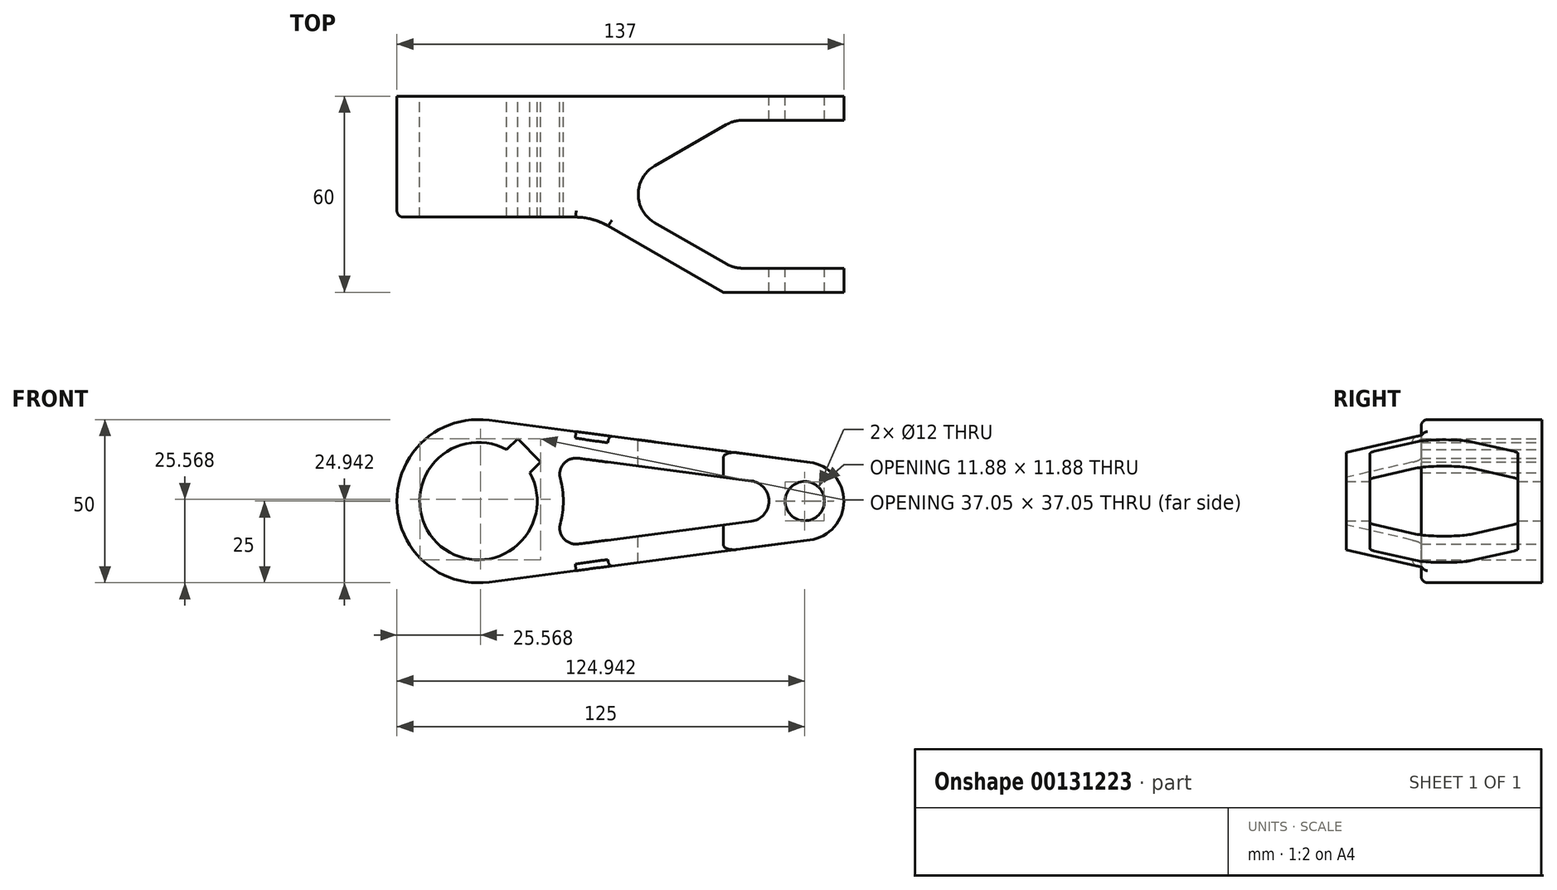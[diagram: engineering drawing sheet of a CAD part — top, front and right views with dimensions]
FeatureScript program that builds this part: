
annotation { "Feature Type Name" : "Feature", "Feature Type Description" : "" }
export const myFeature = defineFeature(function(context is Context, id is Id, definition is map)
    precondition{}
    {
        {
            var Q0;
            Q0=qCreatedBy(makeId("Front.planeOp"),FACE);
            var sketch = newSketch(context, id + "F0", { "sketchPlane" : qUnion([Q0])});
            skArc(sketch, "E0", {"start": v(3.25, 24.79) * mm, "mid": v(-25, 0) * mm, "end": v(3.25, -24.79) * mm});
            skArc(sketch, "E1", {"start": v(101.56, -11.9) * mm, "mid": v(112, 0) * mm, "end": v(101.56, 11.9) * mm});
            skLineSegment(sketch, "E2", {"start": v(0, 0) * mm, "end": v(100, 0) * mm, "construction": true});
            skLineSegment(sketch, "E3", {"start": v(3.25, 24.79) * mm, "end": v(101.56, 11.9) * mm});
            skLineSegment(sketch, "E4", {"start": v(3.25, -24.79) * mm, "end": v(101.56, -11.9) * mm});
            skArc(sketch, "E5", {"start": v(8.7, 15.76) * mm, "mid": v(-12.73, -12.73) * mm, "end": v(15.76, 8.7) * mm});
            skCircle(sketch, "E6", {"center": v(100, 0) * mm, "radius": 6 * mm});
            skLineSegment(sketch, "E7.0", {"start": v(30.55, 13.14) * mm, "end": v(83.57, 6.19) * mm});
            skArc(sketch, "E8.0", {"start": v(26, 0) * mm, "mid": v(25.77, 3.46) * mm, "end": v(25.08, 6.86) * mm});
            skPoint(sketch, "E9.visualSharp", {"position": v(21.72, 14.3) * mm});
            skArc(sketch, "E9.filletArc", {"start": v(30.55, 13.14) * mm, "mid": v(26.13, 11.47) * mm, "end": v(25.08, 6.86) * mm});
            skArc(sketch, "E10", {"start": v(89, 0) * mm, "mid": v(87.45, 4.12) * mm, "end": v(83.57, 6.19) * mm});
            skArc(sketch, "E11.MirrorCS", {"start": v(89, 0) * mm, "mid": v(87.45, -4.12) * mm, "end": v(83.57, -6.19) * mm});
            skLineSegment(sketch, "E12.MirrorCS", {"start": v(30.55, -13.14) * mm, "end": v(83.57, -6.19) * mm});
            skArc(sketch, "E13.MirrorCS", {"start": v(30.55, -13.14) * mm, "mid": v(26.13, -11.47) * mm, "end": v(25.08, -6.86) * mm});
            skArc(sketch, "E14.MirrorCS", {"start": v(26, 0) * mm, "mid": v(25.77, -3.46) * mm, "end": v(25.08, -6.86) * mm});
            skLineSegment(sketch, "E15", {"start": v(0, 0) * mm, "end": v(17.17, 17.17) * mm, "construction": true});
            skLineSegment(sketch, "E16", {"start": v(15.76, 8.7) * mm, "end": v(19.1, 12.02) * mm});
            skLineSegment(sketch, "E17", {"start": v(12.02, 19.1) * mm, "end": v(8.7, 15.76) * mm});
            skLineSegment(sketch, "E18", {"start": v(12.02, 19.1) * mm, "end": v(19.1, 12.02) * mm});
            skSolve(sketch);
        }
        {
            var Q0;
            Q0 = qSketchRegion(id + "F0", true);
            extrude(context, id + "F1", {"entities" : qUnion([Q0]), "endBound" : BoundingType.SYMMETRIC, "depth" : 60 * mm});
        }
        {
            var Q0;
            Q0=qCreatedBy(makeId("Top.planeOp"),FACE);
            var sketch = newSketch(context, id + "F2", { "sketchPlane" : qUnion([Q0])});
            skLineSegment(sketch, "E19", {"start": v(-36.02, 0) * mm, "end": v(127.3, 0) * mm, "construction": true});
            skLineSegment(sketch, "E20", {"start": v(-25, -7) * mm, "end": v(35, -7) * mm});
            skLineSegment(sketch, "E21", {"start": v(35, -7) * mm, "end": v(75, -30) * mm});
            skLineSegment(sketch, "E22", {"start": v(-25, -30) * mm, "end": v(-25, 30) * mm, "construction": true});
            skLineSegment(sketch, "E23", {"start": v(-25, -7) * mm, "end": v(-25, -30) * mm});
            skLineSegment(sketch, "E24", {"start": v(75, -30) * mm, "end": v(-25, -30) * mm});
            skSolve(sketch);
        }
        {
            var Q0;
            Q0 = qSketchRegion(id + "F2", true);
            extrude(context, id + "F3", {"entities" : qUnion([Q0]), "operationType" : NewBodyOperationType.REMOVE, "endBound" : BoundingType.THROUGH_ALL, "oppositeDirection" : true, "depth" : 25 * mm, "hasSecondDirection" : true, "secondDirectionBound" : SecondDirectionBoundingType.THROUGH_ALL, "secondDirectionOppositeDirection" : false, "secondDirectionDepth" : 25 * mm});
        }
        {
            var Q0;
            Q0=qCreatedBy(makeId("Top.planeOp"),FACE);
            var sketch = newSketch(context, id + "F4", { "sketchPlane" : qUnion([Q0])});
            skLineSegment(sketch, "E25.0.0", {"start": v(101.56, 30) * mm, "end": v(112, 30) * mm, "construction": true});
            skLineSegment(sketch, "E25.0.1", {"start": v(101.56, 30) * mm, "end": v(101.56, -30) * mm, "construction": true});
            skLineSegment(sketch, "E25.0.2", {"start": v(101.56, -30) * mm, "end": v(112, -30) * mm, "construction": true});
            skLineSegment(sketch, "E25.0.3", {"start": v(101.56, -30) * mm, "end": v(101.56, 30) * mm, "construction": true});
            skLineSegment(sketch, "E26", {"start": v(112, 30) * mm, "end": v(112, -30) * mm, "construction": true});
            skLineSegment(sketch, "E27", {"start": v(112, -22.65) * mm, "end": v(78.27, -22.65) * mm});
            skLineSegment(sketch, "E28", {"start": v(78.27, -22.65) * mm, "end": v(38.88, 0) * mm});
            skLineSegment(sketch, "E29", {"start": v(38.88, 0) * mm, "end": v(0, 0) * mm, "construction": true});
            skLineSegment(sketch, "E30.MirrorCS", {"start": v(78.27, 22.65) * mm, "end": v(38.88, 0) * mm});
            skLineSegment(sketch, "E31.MirrorCS", {"start": v(112, 22.65) * mm, "end": v(78.27, 22.65) * mm});
            skLineSegment(sketch, "E32", {"start": v(112, 22.65) * mm, "end": v(112, -22.65) * mm});
            skSolve(sketch);
        }
        {
            var Q0;
            Q0 = qSketchRegion(id + "F4", true);
            extrude(context, id + "F5", {"entities" : qUnion([Q0]), "operationType" : NewBodyOperationType.REMOVE, "endBound" : BoundingType.THROUGH_ALL, "oppositeDirection" : true, "depth" : 25 * mm, "hasSecondDirection" : true, "secondDirectionBound" : SecondDirectionBoundingType.THROUGH_ALL, "secondDirectionOppositeDirection" : false, "secondDirectionDepth" : 25 * mm});
        }
        {
            var Q0;
            Q0=makeQuery(id+"F5.boolean.opBoolean","COPY",EDGE,{"disambiguationData":[OD(0.0)],"derivedFrom":makeQuery(id+"F5.opExtrude","SWEPT_EDGE",EDGE,{"disambiguationData":[OSD([sQuery(id+"F4.wireOp",EDGE,"E28"),sQuery(id+"F4.wireOp",EDGE,"E30.MirrorCS")])]})});
            var Q1;
            Q1=makeQuery(id+"F5.boolean.opBoolean","COPY",EDGE,{"disambiguationData":[OD(0.0)],"derivedFrom":makeQuery(id+"F5.opExtrude","SWEPT_EDGE",EDGE,{"disambiguationData":[OSD([sQuery(id+"F4.wireOp",EDGE,"E27"),sQuery(id+"F4.wireOp",EDGE,"E28")])]})});
            var Q2;
            Q2=makeQuery(id+"F5.boolean.opBoolean","COPY",EDGE,{"disambiguationData":[OD(1.0)],"derivedFrom":makeQuery(id+"F5.opExtrude","SWEPT_EDGE",EDGE,{"disambiguationData":[OSD([sQuery(id+"F4.wireOp",EDGE,"E27"),sQuery(id+"F4.wireOp",EDGE,"E28")])]})});
            var Q3;
            Q3=makeQuery(id+"F5.boolean.opBoolean","COPY",EDGE,{"disambiguationData":[OD(0.0)],"derivedFrom":makeQuery(id+"F5.opExtrude","SWEPT_EDGE",EDGE,{"disambiguationData":[OSD([sQuery(id+"F4.wireOp",EDGE,"E30.MirrorCS"),sQuery(id+"F4.wireOp",EDGE,"E31.MirrorCS")])]})});
            var Q4;
            Q4=makeQuery(id+"F5.boolean.opBoolean","COPY",EDGE,{"disambiguationData":[OD(1.0)],"derivedFrom":makeQuery(id+"F5.opExtrude","SWEPT_EDGE",EDGE,{"disambiguationData":[OSD([sQuery(id+"F4.wireOp",EDGE,"E30.MirrorCS"),sQuery(id+"F4.wireOp",EDGE,"E31.MirrorCS")])]})});
            var Q5;
            Q5=makeQuery(id+"F5.boolean.opBoolean","COPY",EDGE,{"disambiguationData":[OD(1.0)],"derivedFrom":makeQuery(id+"F5.opExtrude","SWEPT_EDGE",EDGE,{"disambiguationData":[OSD([sQuery(id+"F4.wireOp",EDGE,"E28"),sQuery(id+"F4.wireOp",EDGE,"E30.MirrorCS")])]})});
            fillet(context, id + "F6", {"entities" : qUnion([Q0, Q1, Q2, Q3, Q4, Q5]), "radius" : 10 * mm, "tangentPropagation" : true, "allowEdgeOverflow" : false});
        }
        {
            var Q0;
            Q0=makeQuery(id+"F3.boolean.opBoolean","COPY",EDGE,{"disambiguationData":[OD(0.0)],"derivedFrom":makeQuery(id+"F3.opExtrude","SWEPT_EDGE",EDGE,{"disambiguationData":[OSD([sQuery(id+"F2.wireOp",EDGE,"E20"),sQuery(id+"F2.wireOp",EDGE,"E21")])]})});
            var Q1;
            Q1=makeQuery(id+"F3.boolean.opBoolean","COPY",EDGE,{"disambiguationData":[OD(1.0)],"derivedFrom":makeQuery(id+"F3.opExtrude","SWEPT_EDGE",EDGE,{"disambiguationData":[OSD([sQuery(id+"F2.wireOp",EDGE,"E20"),sQuery(id+"F2.wireOp",EDGE,"E21")])]})});
            var Q2;
            Q2=makeQuery(id+"F3.boolean.opBoolean","COPY",EDGE,{"disambiguationData":[OD(1.0)],"derivedFrom":makeQuery(id+"F3.opExtrude","SWEPT_EDGE",EDGE,{"disambiguationData":[OSD([sQuery(id+"F2.wireOp",EDGE,"E21"),sQuery(id+"F2.wireOp",EDGE,"E24")])]})});
            var Q3;
            Q3=makeQuery(id+"F3.boolean.opBoolean","COPY",EDGE,{"disambiguationData":[OD(0.0)],"derivedFrom":makeQuery(id+"F3.opExtrude","SWEPT_EDGE",EDGE,{"disambiguationData":[OSD([sQuery(id+"F2.wireOp",EDGE,"E21"),sQuery(id+"F2.wireOp",EDGE,"E24")])]})});
            var Q4;
            Q4=makeQuery(id+"FLbMQRUbMm99wUV_1.1.F3.boolean.opBoolean","COPY",EDGE,{"disambiguationData":[OD(0.0)],"derivedFrom":makeQuery(id+"FLbMQRUbMm99wUV_1.1.F3.opExtrude","SWEPT_EDGE",EDGE,{"disambiguationData":[OSD([sQuery(id+"F2.wireOp",EDGE,"E20"),sQuery(id+"F2.wireOp",EDGE,"E21")])]})});
            var Q5;
            Q5=makeQuery(id+"FLbMQRUbMm99wUV_1.1.F3.boolean.opBoolean","COPY",EDGE,{"disambiguationData":[OD(1.0)],"derivedFrom":makeQuery(id+"FLbMQRUbMm99wUV_1.1.F3.opExtrude","SWEPT_EDGE",EDGE,{"disambiguationData":[OSD([sQuery(id+"F2.wireOp",EDGE,"E20"),sQuery(id+"F2.wireOp",EDGE,"E21")])]})});
            var Q6;
            Q6=makeQuery(id+"FLbMQRUbMm99wUV_1.1.F3.boolean.opBoolean","COPY",EDGE,{"disambiguationData":[OD(0.0)],"derivedFrom":makeQuery(id+"FLbMQRUbMm99wUV_1.1.F3.opExtrude","SWEPT_EDGE",EDGE,{"disambiguationData":[OSD([sQuery(id+"F2.wireOp",EDGE,"E21"),sQuery(id+"F2.wireOp",EDGE,"E24")])]})});
            var Q7;
            Q7=makeQuery(id+"FLbMQRUbMm99wUV_1.1.F3.boolean.opBoolean","COPY",EDGE,{"disambiguationData":[OD(1.0)],"derivedFrom":makeQuery(id+"FLbMQRUbMm99wUV_1.1.F3.opExtrude","SWEPT_EDGE",EDGE,{"disambiguationData":[OSD([sQuery(id+"F2.wireOp",EDGE,"E21"),sQuery(id+"F2.wireOp",EDGE,"E24")])]})});
            fillet(context, id + "F7", {"entities" : qUnion([Q0, Q1, Q2, Q3, Q4, Q5, Q6, Q7]), "radius" : 20 * mm, "tangentPropagation" : true, "allowEdgeOverflow" : false});
        }
        {
            var Q0;
            Q0=makeQuery(id+"F3.boolean.opBoolean","INTERSECT",EDGE,{"derivedFrom":[makeQuery(id+"F1.opExtrude","SWEPT_FACE",FACE,{"disambiguationData":[OSD([sQuery(id+"F0.wireOp",EDGE,"E3")])]}),makeQuery(id+"F3.opExtrude","SWEPT_FACE",FACE,{"disambiguationData":[OSD([sQuery(id+"F2.wireOp",EDGE,"E20")])]})]});
            var Q1;
            Q1=makeQuery(id+"FLbMQRUbMm99wUV_1.1.F3.boolean.opBoolean","INTERSECT",EDGE,{"derivedFrom":[makeQuery(id+"F1.opExtrude","SWEPT_FACE",FACE,{"disambiguationData":[OSD([sQuery(id+"F0.wireOp",EDGE,"E3")])]}),makeQuery(id+"FLbMQRUbMm99wUV_1.1.F3.opExtrude","SWEPT_FACE",FACE,{"disambiguationData":[OSD([sQuery(id+"F2.wireOp",EDGE,"E21")])]})]});
            fillet(context, id + "F8", {"entities" : qUnion([Q0, Q1]), "radius" : 2 * mm, "tangentPropagation" : true, "allowEdgeOverflow" : false});
        }
    });
